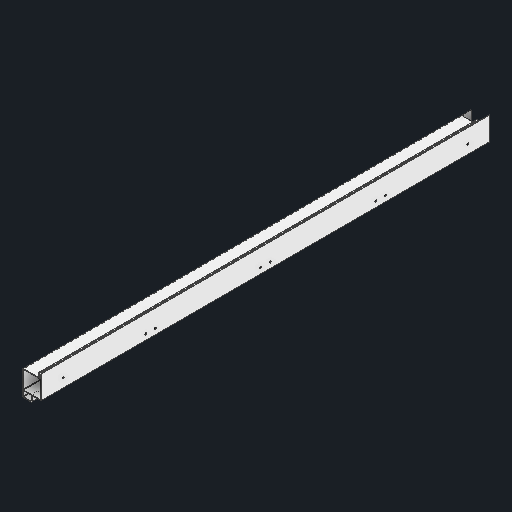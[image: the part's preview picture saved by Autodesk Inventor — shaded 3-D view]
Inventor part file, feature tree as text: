
AUTODESK INVENTOR PART (.ipt)
format: ipt  version: 2025 (Build 290162000, 162)  size: 154,624 bytes
history: native  units: in
note: dims shown in document units (in); Inventor stores cm internally (conversion verified against a paired STEP export)
features: fillet x1
ambient origin geometry x8: Origin, YZ Plane, XZ Plane, XY Plane, X Axis, Y Axis, Z Axis, Center Point
bodies: Solid1 (feature_tree)
feature tree (1):
  fillet  "Fillet6"  [1 undecoded]
note: 1 required parameter value undecoded (feature->parameter linkage not recoverable at this tier; creation-order binding heuristic only, values carry confidence <= 0.55)
